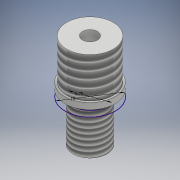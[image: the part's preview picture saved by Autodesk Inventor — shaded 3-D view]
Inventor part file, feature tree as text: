
AUTODESK INVENTOR PART (.ipt)
format: ipt  version: 2017 (Build 210142000, 142)  size: 136,192 bytes
history: native  units: mm
features: sketch x6, extrude x5, thread x2
ambient origin geometry x8: Origin, YZ Plane, XZ Plane, XY Plane, X Axis, Y Axis, Z Axis, Center Point
bodies: Solid1 (feature_tree)
feature tree (13):
  extrude  "Extrusion1"  Depth=18.75mm TaperAngle=0.0deg
  extrude  "Extrusion2"  Depth=8.0mm TaperAngle=0.0deg
  extrude  "Extrusion3"  Depth=50.0mm TaperAngle=0.0deg
  extrude  "Extrusion4"  Depth=10.0mm
  sketch  "Sketch5"  dims[d14=10.0mm d15=10.0mm d16=0.0mm]
  thread  "Thread1"  [1 undecoded]
  thread  "Thread2"  [1 undecoded]
  extrude  "Extrusion5"  Depth=10.0mm TaperAngle=0.0deg
  sketch  "Sketch1"  dims[d0=10.0mm d1=18.75mm d2=0.0mm]
  sketch  "Sketch2"  dims[d3=9.25mm d4=8.0mm d5=0.0mm]
  sketch  "Sketch3"  dims[d6=3.0mm d7=50.0mm d8=0.0mm]
  sketch  "Sketch4"  dims[d9=6.75mm d10=10.0mm d11=8.25mm d12=0.0mm d13=6.75mm]
  sketch  "Sketch6"  dims[d17=10.0mm d18=0.0mm d19=1.25mm d20=0.0mm]
note: 2 required parameter values undecoded (feature->parameter linkage not recoverable at this tier; creation-order binding heuristic only, values carry confidence <= 0.55)
